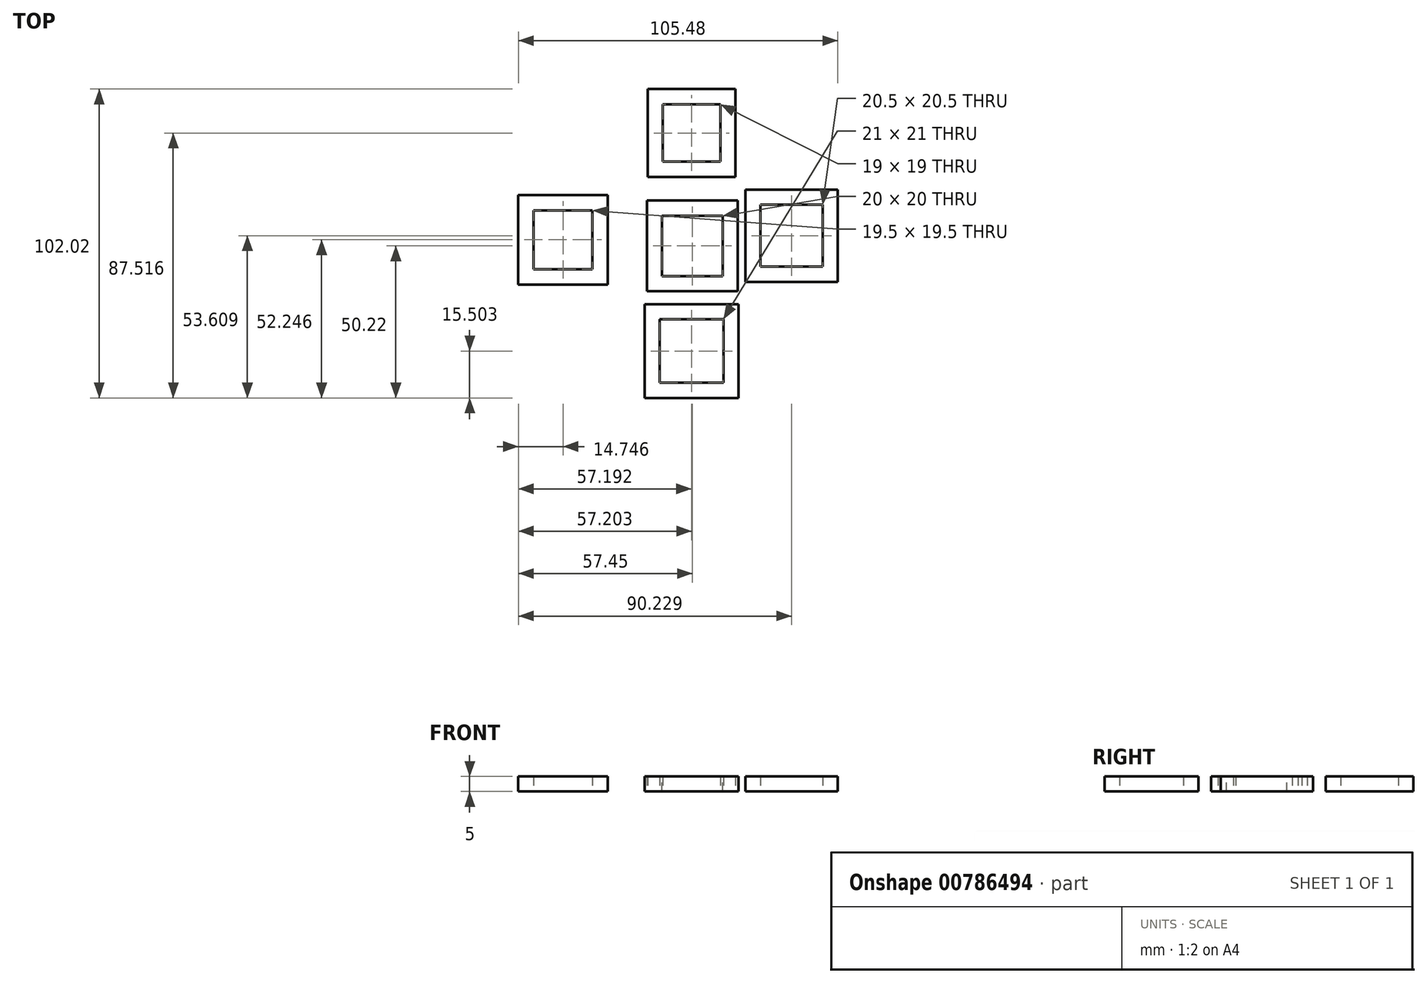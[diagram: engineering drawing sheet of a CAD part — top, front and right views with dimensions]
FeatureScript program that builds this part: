
annotation { "Feature Type Name" : "Feature", "Feature Type Description" : "" }
export const myFeature = defineFeature(function(context is Context, id is Id, definition is map)
    precondition{}
    {
        {
            var Q0;
            Q0=qCreatedBy(makeId("Top.planeOp"),FACE);
            var sketch = newSketch(context, id + "F0", { "sketchPlane" : qUnion([Q0])});
            skLineSegment(sketch, "E0.bottom", {"start": v(-15, 15) * mm, "end": v(15, 15) * mm});
            skLineSegment(sketch, "E0.top", {"start": v(-15, -15) * mm, "end": v(15, -15) * mm});
            skLineSegment(sketch, "E0.left", {"start": v(-15, 15) * mm, "end": v(-15, -15) * mm});
            skLineSegment(sketch, "E0.right", {"start": v(15, 15) * mm, "end": v(15, -15) * mm});
            skSolve(sketch);
        }
        {
            var Q0;
            Q0 = qSketchRegion(id + "F0", true);
            extrude(context, id + "F1", {"entities" : qUnion([Q0]), "depth" : 5 * mm, "offsetDistance" : 25 * mm});
        }
        {
            var Q0;
            Q0=makeQuery(id+"F1.opExtrude","CAP_FACE",FACE,{"disambiguationData":[OSD([sQuery(id+"F0.wireOp",EDGE,"E0.bottom"),sQuery(id+"F0.wireOp",EDGE,"E0.top"),sQuery(id+"F0.wireOp",EDGE,"E0.left"),sQuery(id+"F0.wireOp",EDGE,"E0.right")])],"isStart":false});
            var sketch = newSketch(context, id + "F2", { "sketchPlane" : qUnion([Q0])});
            skLineSegment(sketch, "E1.bottom", {"start": v(-10, 10) * mm, "end": v(10, 10) * mm});
            skLineSegment(sketch, "E1.top", {"start": v(-10, -10) * mm, "end": v(10, -10) * mm});
            skLineSegment(sketch, "E1.left", {"start": v(-10, 10) * mm, "end": v(-10, -10) * mm});
            skLineSegment(sketch, "E1.right", {"start": v(10, 10) * mm, "end": v(10, -10) * mm});
            skSolve(sketch);
        }
        {
            var Q0;
            Q0 = qSketchRegion(id + "F2", true);
            extrude(context, id + "F3", {"entities" : qUnion([Q0]), "operationType" : NewBodyOperationType.REMOVE, "oppositeDirection" : true, "depth" : 5 * mm, "offsetDistance" : 25 * mm});
        }
        {
            var Q0;
            Q0=qCreatedBy(makeId("Top.planeOp"),FACE);
            var sketch = newSketch(context, id + "F4", { "sketchPlane" : qUnion([Q0])});
            skLineSegment(sketch, "E2.bottom", {"start": v(-14.75, 51.8) * mm, "end": v(14.25, 51.8) * mm});
            skLineSegment(sketch, "E2.top", {"start": v(-14.75, 22.8) * mm, "end": v(14.25, 22.8) * mm});
            skLineSegment(sketch, "E2.left", {"start": v(-14.75, 51.8) * mm, "end": v(-14.75, 22.8) * mm});
            skLineSegment(sketch, "E2.right", {"start": v(14.25, 51.8) * mm, "end": v(14.25, 22.8) * mm});
            skLineSegment(sketch, "E3.bottom", {"start": v(-9.75, 46.8) * mm, "end": v(9.25, 46.8) * mm});
            skLineSegment(sketch, "E3.top", {"start": v(-9.75, 27.8) * mm, "end": v(9.25, 27.8) * mm});
            skLineSegment(sketch, "E3.left", {"start": v(-9.75, 46.8) * mm, "end": v(-9.75, 27.8) * mm});
            skLineSegment(sketch, "E3.right", {"start": v(9.25, 46.8) * mm, "end": v(9.25, 27.8) * mm});
            skSolve(sketch);
        }
        {
            var Q0;
            Q0=makeQuery(id+"F4.imprint","IMPRINT",FACE,{"disambiguationData":[TD([[makeQuery(id+"F4.imprint","IMPRINT",EDGE,{"derivedFrom":sQuery(id+"F4.wireOp",EDGE,"E2.bottom")}),-1.0]])]});
            extrude(context, id + "F5", {"entities" : qUnion([Q0]), "depth" : 5 * mm, "offsetDistance" : 25 * mm});
        }
        {
            var Q0;
            Q0=qCreatedBy(makeId("Top.planeOp"),FACE);
            var sketch = newSketch(context, id + "F6", { "sketchPlane" : qUnion([Q0])});
            skLineSegment(sketch, "E4.bottom", {"start": v(-15.76, -19.22) * mm, "end": v(15.24, -19.22) * mm});
            skLineSegment(sketch, "E4.top", {"start": v(-15.76, -50.22) * mm, "end": v(15.24, -50.22) * mm});
            skLineSegment(sketch, "E4.left", {"start": v(-15.76, -19.22) * mm, "end": v(-15.76, -50.22) * mm});
            skLineSegment(sketch, "E4.right", {"start": v(15.24, -19.22) * mm, "end": v(15.24, -50.22) * mm});
            skLineSegment(sketch, "E5.bottom", {"start": v(-10.76, -24.22) * mm, "end": v(10.24, -24.22) * mm});
            skLineSegment(sketch, "E5.top", {"start": v(-10.76, -45.22) * mm, "end": v(10.24, -45.22) * mm});
            skLineSegment(sketch, "E5.left", {"start": v(-10.76, -24.22) * mm, "end": v(-10.76, -45.22) * mm});
            skLineSegment(sketch, "E5.right", {"start": v(10.24, -24.22) * mm, "end": v(10.24, -45.22) * mm});
            skSolve(sketch);
        }
        {
            var Q0;
            Q0=makeQuery(id+"F6.imprint","IMPRINT",FACE,{"disambiguationData":[TD([[makeQuery(id+"F6.imprint","IMPRINT",EDGE,{"derivedFrom":sQuery(id+"F6.wireOp",EDGE,"E4.bottom")}),-1.0]])]});
            extrude(context, id + "F7", {"entities" : qUnion([Q0]), "depth" : 5 * mm, "offsetDistance" : 25 * mm});
        }
        {
            var Q0;
            Q0=qCreatedBy(makeId("Top.planeOp"),FACE);
            var sketch = newSketch(context, id + "F8", { "sketchPlane" : qUnion([Q0])});
            skLineSegment(sketch, "E6.bottom", {"start": v(17.53, 18.64) * mm, "end": v(48.03, 18.64) * mm});
            skLineSegment(sketch, "E6.top", {"start": v(17.53, -11.86) * mm, "end": v(48.03, -11.86) * mm});
            skLineSegment(sketch, "E6.left", {"start": v(17.53, 18.64) * mm, "end": v(17.53, -11.86) * mm});
            skLineSegment(sketch, "E6.right", {"start": v(48.03, 18.64) * mm, "end": v(48.03, -11.86) * mm});
            skLineSegment(sketch, "E7.bottom", {"start": v(22.53, 13.64) * mm, "end": v(43.03, 13.64) * mm});
            skLineSegment(sketch, "E7.top", {"start": v(22.53, -6.86) * mm, "end": v(43.03, -6.86) * mm});
            skLineSegment(sketch, "E7.left", {"start": v(22.53, 13.64) * mm, "end": v(22.53, -6.86) * mm});
            skLineSegment(sketch, "E7.right", {"start": v(43.03, 13.64) * mm, "end": v(43.03, -6.86) * mm});
            skSolve(sketch);
        }
        {
            var Q0;
            Q0=makeQuery(id+"F8.imprint","IMPRINT",FACE,{"disambiguationData":[TD([[makeQuery(id+"F8.imprint","IMPRINT",EDGE,{"derivedFrom":sQuery(id+"F8.wireOp",EDGE,"E6.bottom")}),-1.0]])]});
            extrude(context, id + "F9", {"entities" : qUnion([Q0]), "depth" : 5 * mm, "offsetDistance" : 25 * mm});
        }
        {
            var Q0;
            Q0=qCreatedBy(makeId("Top.planeOp"),FACE);
            var sketch = newSketch(context, id + "F10", { "sketchPlane" : qUnion([Q0])});
            skLineSegment(sketch, "E8.bottom", {"start": v(-57.45, 16.78) * mm, "end": v(-27.95, 16.78) * mm});
            skLineSegment(sketch, "E8.top", {"start": v(-57.45, -12.72) * mm, "end": v(-27.95, -12.72) * mm});
            skLineSegment(sketch, "E8.left", {"start": v(-57.45, 16.78) * mm, "end": v(-57.45, -12.72) * mm});
            skLineSegment(sketch, "E8.right", {"start": v(-27.95, 16.78) * mm, "end": v(-27.95, -12.72) * mm});
            skLineSegment(sketch, "E9.bottom", {"start": v(-52.45, 11.78) * mm, "end": v(-32.95, 11.78) * mm});
            skLineSegment(sketch, "E9.top", {"start": v(-52.45, -7.72) * mm, "end": v(-32.95, -7.72) * mm});
            skLineSegment(sketch, "E9.left", {"start": v(-52.45, 11.78) * mm, "end": v(-52.45, -7.72) * mm});
            skLineSegment(sketch, "E9.right", {"start": v(-32.95, 11.78) * mm, "end": v(-32.95, -7.72) * mm});
            skSolve(sketch);
        }
        {
            var Q0;
            Q0=makeQuery(id+"F10.imprint","IMPRINT",FACE,{"disambiguationData":[TD([[makeQuery(id+"F10.imprint","IMPRINT",EDGE,{"derivedFrom":sQuery(id+"F10.wireOp",EDGE,"E8.bottom")}),-1.0]])]});
            extrude(context, id + "F11", {"entities" : qUnion([Q0]), "depth" : 5 * mm, "offsetDistance" : 25 * mm});
        }
    });
